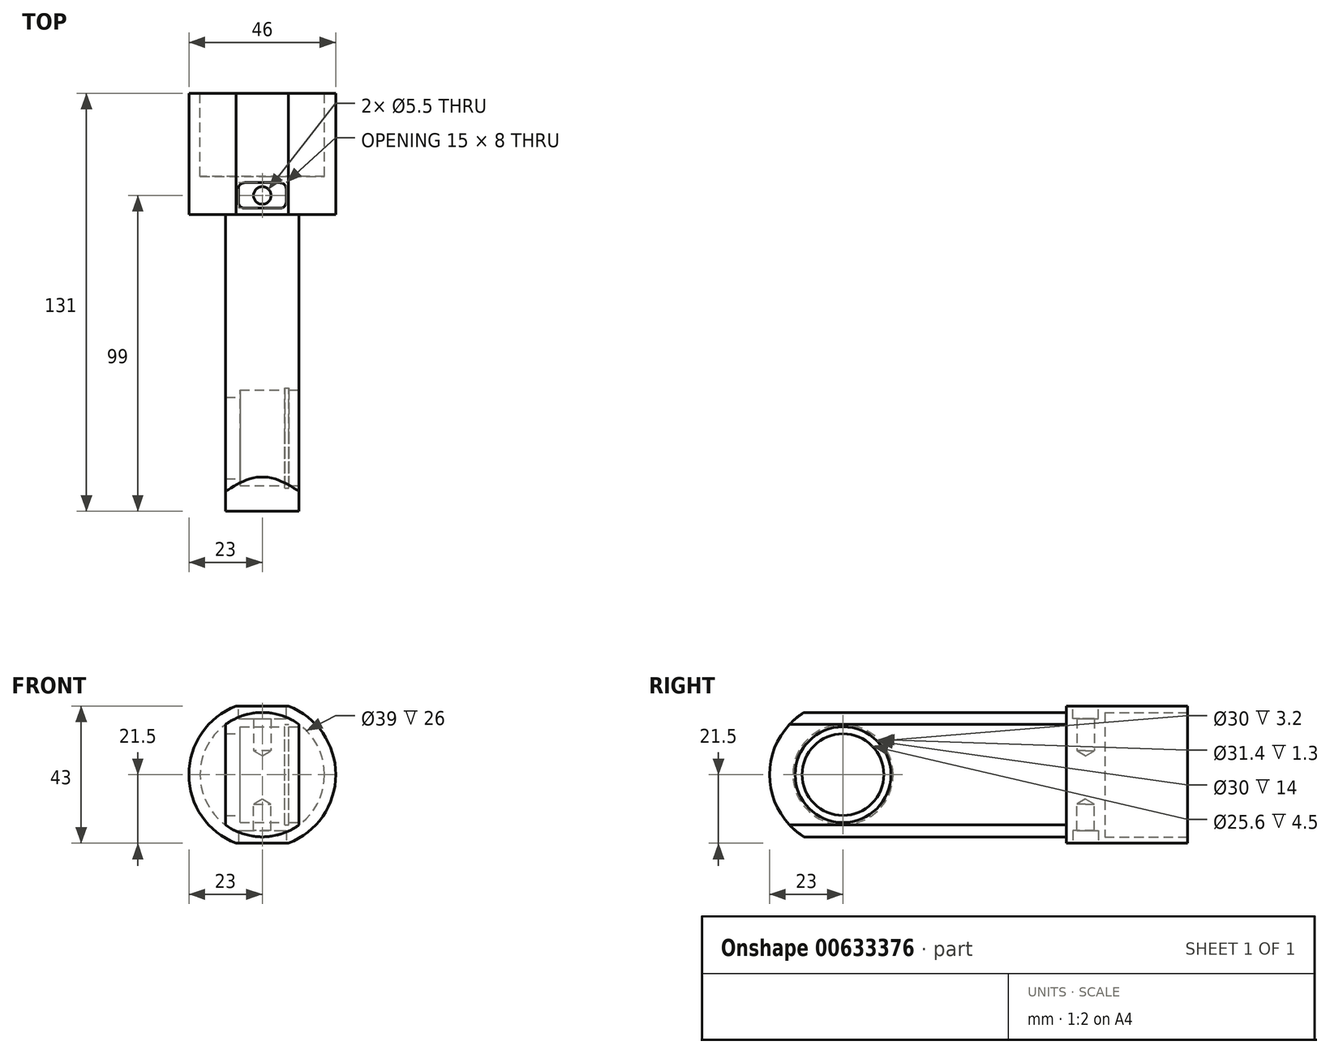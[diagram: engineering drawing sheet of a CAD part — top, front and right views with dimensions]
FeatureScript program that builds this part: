
annotation { "Feature Type Name" : "Feature", "Feature Type Description" : "" }
export const myFeature = defineFeature(function(context is Context, id is Id, definition is map)
    precondition{}
    {
        {
            var Q0;
            Q0=qCreatedBy(makeId("Front.planeOp"),FACE);
            var sketch = newSketch(context, id + "F0", { "sketchPlane" : qUnion([Q0])});
            skArc(sketch, "E0", {"start": v(-8.17, 21.5) * mm, "mid": v(-23, 0) * mm, "end": v(-8.17, -21.5) * mm});
            skLineSegment(sketch, "E1", {"start": v(-8.17, 21.5) * mm, "end": v(8.17, 21.5) * mm});
            skLineSegment(sketch, "E2.MirrorCS", {"start": v(-8.17, -21.5) * mm, "end": v(8.17, -21.5) * mm});
            skArc(sketch, "E3.trimOffspring", {"start": v(8.17, -21.5) * mm, "mid": v(23, 0) * mm, "end": v(8.17, 21.5) * mm});
            skSolve(sketch);
        }
        {
            var Q0;
            Q0 = qSketchRegion(id + "F0", true);
            extrude(context, id + "F1", {"entities" : qUnion([Q0]), "depth" : (32 + 6) * mm, "offsetDistance" : 25 * mm});
        }
        {
            var Q0;
            Q0=makeQuery(id+"F1.opExtrude","CAP_FACE",FACE,{"disambiguationData":[OSD([sQuery(id+"F0.wireOp",EDGE,"E0"),sQuery(id+"F0.wireOp",EDGE,"E1"),sQuery(id+"F0.wireOp",EDGE,"E2.MirrorCS"),sQuery(id+"F0.wireOp",EDGE,"E3.trimOffspring")])],"isStart":false});
            var sketch = newSketch(context, id + "F2", { "sketchPlane" : qUnion([Q0])});
            skArc(sketch, "E4", {"start": v(-11.5, -15.75) * mm, "mid": v(0, -19.5) * mm, "end": v(11.5, -15.75) * mm});
            skLineSegment(sketch, "E5", {"start": v(-11.5, 15.75) * mm, "end": v(-11.5, -15.75) * mm});
            skLineSegment(sketch, "E6.MirrorCS", {"start": v(11.5, 15.75) * mm, "end": v(11.5, -15.75) * mm});
            skArc(sketch, "E7.trimOffspring", {"start": v(11.5, 15.75) * mm, "mid": v(0, 19.5) * mm, "end": v(-11.5, 15.75) * mm});
            skSolve(sketch);
        }
        {
            var Q0;
            Q0 = qSketchRegion(id + "F2", true);
            extrude(context, id + "F3", {"entities" : qUnion([Q0]), "operationType" : NewBodyOperationType.ADD, "depth" : 93 * mm, "offsetDistance" : 25 * mm});
        }
        {
            var Q0;
            Q0=makeQuery(id+"F3.opExtrude","SWEPT_FACE",FACE,{"disambiguationData":[OSD([sQuery(id+"F2.wireOp",EDGE,"E6.MirrorCS")])]});
            var sketch = newSketch(context, id + "F4", { "sketchPlane" : qUnion([Q0])});
            skArc(sketch, "E8", {"start": v(-107.6, 23) * mm, "mid": v(-130.94, 1.66) * mm, "end": v(-110.91, -22.81) * mm});
            skLineSegment(sketch, "E9", {"start": v(-107.6, 23) * mm, "end": v(-137.6, 23) * mm});
            skLineSegment(sketch, "E10", {"start": v(-137.6, 23) * mm, "end": v(-137.6, -22.41) * mm});
            skLineSegment(sketch, "E11", {"start": v(-137.6, -22.41) * mm, "end": v(-110.91, -22.81) * mm});
            skSolve(sketch);
        }
        {
            var Q0;
            Q0 = qSketchRegion(id + "F4", true);
            extrude(context, id + "F5", {"entities" : qUnion([Q0]), "operationType" : NewBodyOperationType.REMOVE, "endBound" : BoundingType.THROUGH_ALL, "oppositeDirection" : true, "depth" : 25 * mm, "offsetDistance" : 25 * mm});
        }
        {
            var Q0;
            Q0=makeQuery(id+"F1.opExtrude","CAP_FACE",FACE,{"disambiguationData":[OSD([sQuery(id+"F0.wireOp",EDGE,"E0"),sQuery(id+"F0.wireOp",EDGE,"E1"),sQuery(id+"F0.wireOp",EDGE,"E2.MirrorCS"),sQuery(id+"F0.wireOp",EDGE,"E3.trimOffspring")])],"isStart":true});
            var sketch = newSketch(context, id + "F6", { "sketchPlane" : qUnion([Q0])});
            skCircle(sketch, "E12", {"center": v(0, 0) * mm, "radius": 19.5 * mm});
            skSolve(sketch);
        }
        {
            var Q0;
            Q0 = qSketchRegion(id + "F6", true);
            extrude(context, id + "F7", {"entities" : qUnion([Q0]), "operationType" : NewBodyOperationType.REMOVE, "oppositeDirection" : true, "depth" : 26 * mm, "offsetDistance" : 25 * mm});
        }
        {
            var Q0;
            Q0=makeQuery(id+"F3.opExtrude","SWEPT_FACE",FACE,{"disambiguationData":[OSD([sQuery(id+"F2.wireOp",EDGE,"E6.MirrorCS")])]});
            var sketch = newSketch(context, id + "F8", { "sketchPlane" : qUnion([Q0])});
            skCircle(sketch, "E13", {"center": v(-108, 0) * mm, "radius": 15 * mm});
            skSolve(sketch);
        }
        {
            var Q0;
            Q0 = qSketchRegion(id + "F8", true);
            extrude(context, id + "F9", {"entities" : qUnion([Q0]), "operationType" : NewBodyOperationType.REMOVE, "oppositeDirection" : true, "depth" : 3.2 * mm, "offsetDistance" : 25 * mm});
        }
        {
            var Q0;
            Q0=makeQuery(id+"F9.boolean.opBoolean","COPY",FACE,{"derivedFrom":makeQuery(id+"F9.opExtrude","CAP_FACE",FACE,{"disambiguationData":[OSD([sQuery(id+"F8.wireOp",EDGE,"E13")])],"isStart":false})});
            var sketch = newSketch(context, id + "F10", { "sketchPlane" : qUnion([Q0])});
            skCircle(sketch, "E14", {"center": v(-108, 0) * mm, "radius": 15.7 * mm});
            skSolve(sketch);
        }
        {
            var Q0;
            Q0 = qSketchRegion(id + "F10", true);
            extrude(context, id + "F11", {"entities" : qUnion([Q0]), "operationType" : NewBodyOperationType.REMOVE, "oppositeDirection" : true, "depth" : 1.3 * mm, "offsetDistance" : 25 * mm});
        }
        {
            var Q0;
            Q0=makeQuery(id+"F11.boolean.opBoolean","COPY",FACE,{"derivedFrom":makeQuery(id+"F11.opExtrude","CAP_FACE",FACE,{"disambiguationData":[OSD([sQuery(id+"F10.wireOp",EDGE,"E14")])],"isStart":false})});
            var sketch = newSketch(context, id + "F12", { "sketchPlane" : qUnion([Q0])});
            skCircle(sketch, "E15", {"center": v(-108, 0) * mm, "radius": 15 * mm});
            skSolve(sketch);
        }
        {
            var Q0;
            Q0 = qSketchRegion(id + "F12", true);
            extrude(context, id + "F13", {"entities" : qUnion([Q0]), "operationType" : NewBodyOperationType.REMOVE, "oppositeDirection" : true, "depth" : 14 * mm, "offsetDistance" : 25 * mm});
        }
        {
            var Q0;
            Q0=makeQuery(id+"F13.boolean.opBoolean","COPY",FACE,{"derivedFrom":makeQuery(id+"F13.opExtrude","CAP_FACE",FACE,{"disambiguationData":[OSD([sQuery(id+"F12.wireOp",EDGE,"E15")])],"isStart":false})});
            var sketch = newSketch(context, id + "F14", { "sketchPlane" : qUnion([Q0])});
            skCircle(sketch, "E16", {"center": v(-108, 0) * mm, "radius": 12.8 * mm});
            skSolve(sketch);
        }
        {
            var Q0;
            Q0 = qSketchRegion(id + "F14", true);
            extrude(context, id + "F15", {"entities" : qUnion([Q0]), "operationType" : NewBodyOperationType.REMOVE, "endBound" : BoundingType.THROUGH_ALL, "oppositeDirection" : true, "depth" : 25 * mm, "offsetDistance" : 25 * mm});
        }
        {
            var Q0;
            Q0=makeQuery(id+"F1.opExtrude","SWEPT_FACE",FACE,{"disambiguationData":[OSD([sQuery(id+"F0.wireOp",EDGE,"E1")])]});
            var sketch = newSketch(context, id + "F16", { "sketchPlane" : qUnion([Q0])});
            skLineSegment(sketch, "E17.bottom", {"start": v(-5.5, -28) * mm, "end": v(5.5, -28) * mm});
            skLineSegment(sketch, "E17.top", {"start": v(-5.5, -36) * mm, "end": v(5.5, -36) * mm});
            skLineSegment(sketch, "E17.left", {"start": v(-7.5, -30) * mm, "end": v(-7.5, -34) * mm});
            skLineSegment(sketch, "E17.right", {"start": v(7.5, -30) * mm, "end": v(7.5, -34) * mm});
            skPoint(sketch, "E17.middle", {"position": v(0, -32) * mm});
            skPoint(sketch, "E18.visualSharp", {"position": v(-7.5, -28) * mm});
            skArc(sketch, "E18.filletArc", {"start": v(-5.5, -28) * mm, "mid": v(-6.91, -28.59) * mm, "end": v(-7.5, -30) * mm});
            skPoint(sketch, "E19.visualSharp", {"position": v(-7.5, -36) * mm});
            skArc(sketch, "E19.filletArc", {"start": v(-7.5, -34) * mm, "mid": v(-6.91, -35.41) * mm, "end": v(-5.5, -36) * mm});
            skPoint(sketch, "E20.visualSharp", {"position": v(7.5, -36) * mm});
            skArc(sketch, "E20.filletArc", {"start": v(5.5, -36) * mm, "mid": v(6.91, -35.41) * mm, "end": v(7.5, -34) * mm});
            skPoint(sketch, "E21.visualSharp", {"position": v(7.5, -28) * mm});
            skArc(sketch, "E21.filletArc", {"start": v(7.5, -30) * mm, "mid": v(6.91, -28.59) * mm, "end": v(5.5, -28) * mm});
            skSolve(sketch);
        }
        {
            var Q0;
            Q0 = qSketchRegion(id + "F16", true);
            extrude(context, id + "F17", {"entities" : qUnion([Q0]), "operationType" : NewBodyOperationType.REMOVE, "oppositeDirection" : true, "depth" : 4 * mm, "offsetDistance" : 25 * mm});
        }
        {
            var Q0;
            Q0=makeQuery(id+"F17.boolean.opBoolean","COPY",FACE,{"derivedFrom":makeQuery(id+"F17.opExtrude","CAP_FACE",FACE,{"disambiguationData":[OSD([sQuery(id+"F16.wireOp",EDGE,"E17.bottom"),sQuery(id+"F16.wireOp",EDGE,"E17.top"),sQuery(id+"F16.wireOp",EDGE,"E17.left"),sQuery(id+"F16.wireOp",EDGE,"E17.right"),sQuery(id+"F16.wireOp",EDGE,"E18.filletArc"),sQuery(id+"F16.wireOp",EDGE,"E19.filletArc"),sQuery(id+"F16.wireOp",EDGE,"E20.filletArc"),sQuery(id+"F16.wireOp",EDGE,"E21.filletArc")])],"isStart":false})});
            var sketch = newSketch(context, id + "F18", { "sketchPlane" : qUnion([Q0])});
            skPoint(sketch, "E22", {"position": v(0, -32) * mm});
            skSolve(sketch);
        }
        {
            var Q0;
            Q0=sQuery(id+"F18.wireOp",VERTEX,"E22");
            var Q1;
            Q1=makeQuery(id+"F1.opExtrude","SWEPT_BODY",BODY,{"disambiguationData":[OSD([sQuery(id+"F0.wireOp",EDGE,"E0"),sQuery(id+"F0.wireOp",EDGE,"E1"),sQuery(id+"F0.wireOp",EDGE,"E2.MirrorCS"),sQuery(id+"F0.wireOp",EDGE,"E3.trimOffspring")])]});
            hole(context, id + "F19", {"style" : HoleStyle.SIMPLE, "endStyle" : HoleEndStyle.BLIND, "standardTappedOrClearance" : lookupTablePath({ "standard" : "ISO", "fit" : "Normal", "size" : "M5", "type" : "Clearance" }), "standardBlindInLast" : lookupTablePath({ "fit" : "Standard", "standard" : "ISO", "size" : "M5", "type" : "Clearance" }), "holeDiameter" : 5.5 * mm, "majorDiameter" : 5 * mm, "holeDepth" : 10 * mm, "isTappedThrough" : true, "tappedDepth" : 5 * mm, "tapClearance" : 5, "startFromSketch" : true, "locations" : qUnion([Q0]), "scope" : qUnion([Q1])});
        }
        {
            var Q0;
            Q0=makeQuery(id+"F1.opExtrude","SWEPT_FACE",FACE,{"disambiguationData":[OSD([sQuery(id+"F0.wireOp",EDGE,"E2.MirrorCS")])]});
            var sketch = newSketch(context, id + "F20", { "sketchPlane" : qUnion([Q0])});
            skLineSegment(sketch, "E23.bottom", {"start": v(-5.5, 36) * mm, "end": v(5.5, 36) * mm});
            skLineSegment(sketch, "E23.top", {"start": v(-5.5, 28) * mm, "end": v(5.5, 28) * mm});
            skLineSegment(sketch, "E23.left", {"start": v(-7.5, 34) * mm, "end": v(-7.5, 30) * mm});
            skLineSegment(sketch, "E23.right", {"start": v(7.5, 34) * mm, "end": v(7.5, 30) * mm});
            skPoint(sketch, "E23.middle", {"position": v(0, 32) * mm});
            skPoint(sketch, "E24.visualSharp", {"position": v(-7.5, 36) * mm});
            skArc(sketch, "E24.filletArc", {"start": v(-5.5, 36) * mm, "mid": v(-6.91, 35.41) * mm, "end": v(-7.5, 34) * mm});
            skPoint(sketch, "E25.visualSharp", {"position": v(-7.5, 28) * mm});
            skArc(sketch, "E25.filletArc", {"start": v(-7.5, 30) * mm, "mid": v(-6.91, 28.59) * mm, "end": v(-5.5, 28) * mm});
            skPoint(sketch, "E26.visualSharp", {"position": v(7.5, 28) * mm});
            skArc(sketch, "E26.filletArc", {"start": v(5.5, 28) * mm, "mid": v(6.91, 28.59) * mm, "end": v(7.5, 30) * mm});
            skPoint(sketch, "E27.visualSharp", {"position": v(7.5, 36) * mm});
            skArc(sketch, "E27.filletArc", {"start": v(7.5, 34) * mm, "mid": v(6.91, 35.41) * mm, "end": v(5.5, 36) * mm});
            skSolve(sketch);
        }
        {
            var Q0;
            Q0 = qSketchRegion(id + "F20", true);
            extrude(context, id + "F21", {"entities" : qUnion([Q0]), "operationType" : NewBodyOperationType.REMOVE, "oppositeDirection" : true, "depth" : 4 * mm, "offsetDistance" : 25 * mm});
        }
        {
            var Q0;
            Q0=makeQuery(id+"F21.boolean.opBoolean","COPY",FACE,{"derivedFrom":makeQuery(id+"F21.opExtrude","CAP_FACE",FACE,{"disambiguationData":[OSD([sQuery(id+"F20.wireOp",EDGE,"E23.bottom"),sQuery(id+"F20.wireOp",EDGE,"E23.top"),sQuery(id+"F20.wireOp",EDGE,"E23.left"),sQuery(id+"F20.wireOp",EDGE,"E23.right"),sQuery(id+"F20.wireOp",EDGE,"E24.filletArc"),sQuery(id+"F20.wireOp",EDGE,"E25.filletArc"),sQuery(id+"F20.wireOp",EDGE,"E26.filletArc"),sQuery(id+"F20.wireOp",EDGE,"E27.filletArc")])],"isStart":false})});
            var sketch = newSketch(context, id + "F22", { "sketchPlane" : qUnion([Q0])});
            skPoint(sketch, "E28", {"position": v(0, 32) * mm});
            skSolve(sketch);
        }
        {
            var Q0;
            Q0=sQuery(id+"F22.wireOp",VERTEX,"E28");
            var Q1;
            Q1=makeQuery(id+"F1.opExtrude","SWEPT_BODY",BODY,{"disambiguationData":[OSD([sQuery(id+"F0.wireOp",EDGE,"E0"),sQuery(id+"F0.wireOp",EDGE,"E1"),sQuery(id+"F0.wireOp",EDGE,"E2.MirrorCS"),sQuery(id+"F0.wireOp",EDGE,"E3.trimOffspring")])]});
            hole(context, id + "F23", {"style" : HoleStyle.SIMPLE, "endStyle" : HoleEndStyle.BLIND, "standardTappedOrClearance" : lookupTablePath({ "standard" : "ISO", "fit" : "Normal", "size" : "M5", "type" : "Clearance" }), "standardBlindInLast" : lookupTablePath({ "fit" : "Standard", "standard" : "ISO", "size" : "M5", "type" : "Clearance" }), "holeDiameter" : 5.5 * mm, "majorDiameter" : 5 * mm, "holeDepth" : 8.2 * mm, "isTappedThrough" : true, "tappedDepth" : 5 * mm, "tapClearance" : 4, "startFromSketch" : true, "locations" : qUnion([Q0]), "scope" : qUnion([Q1])});
        }
    });
